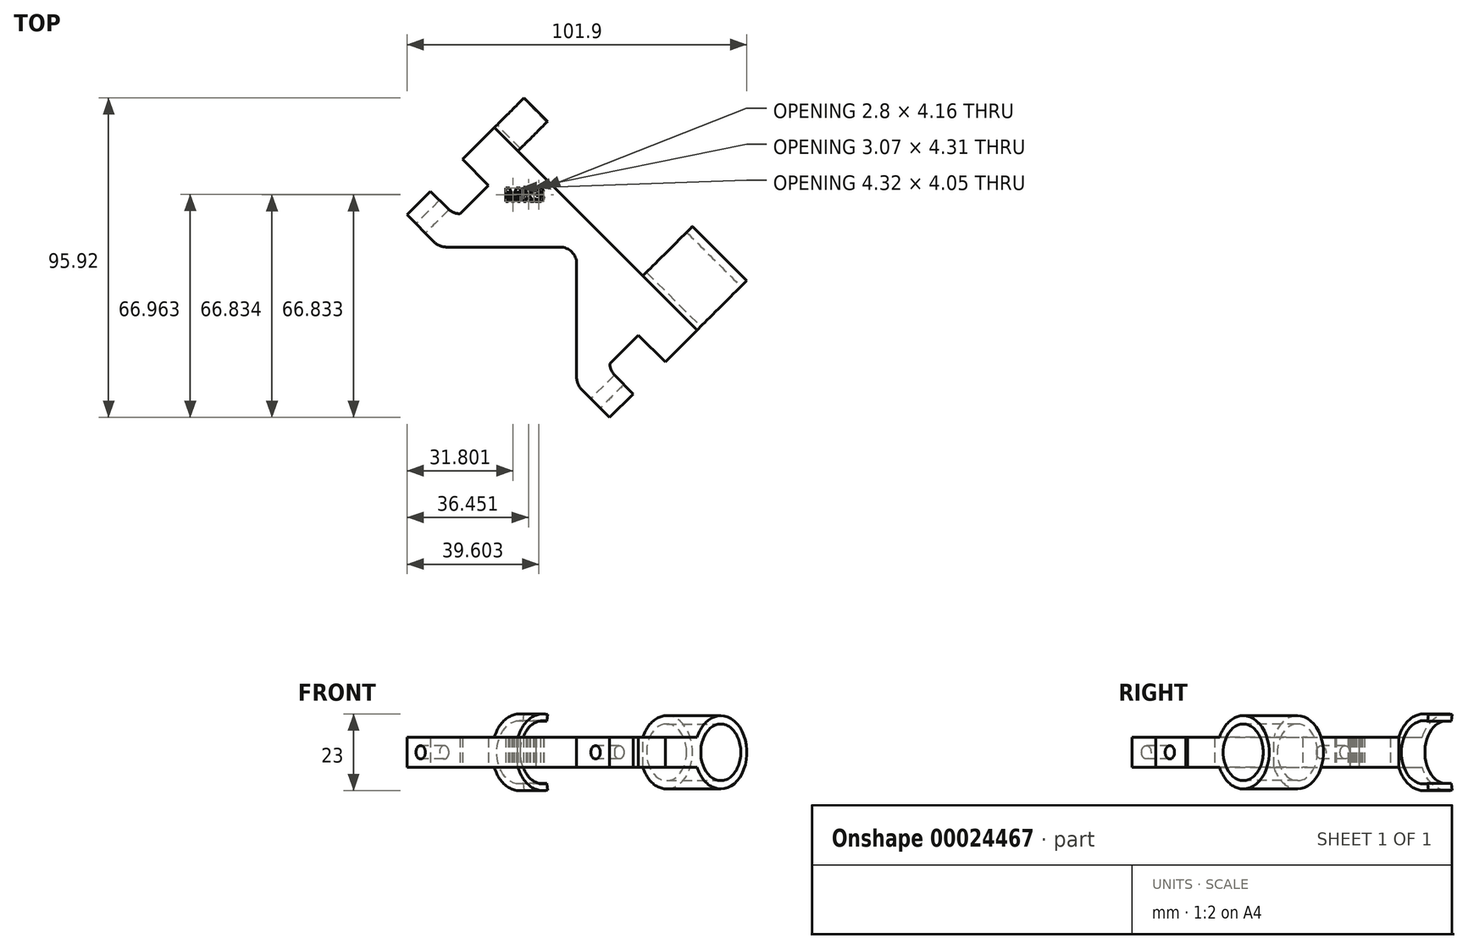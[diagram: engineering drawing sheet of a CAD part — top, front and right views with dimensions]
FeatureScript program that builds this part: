
annotation { "Feature Type Name" : "Feature", "Feature Type Description" : "" }
export const myFeature = defineFeature(function(context is Context, id is Id, definition is map)
    precondition{}
    {
        {
            var Q0;
            Q0=qCreatedBy(makeId("Top.planeOp"),FACE);
            var sketch = newSketch(context, id + "F0", { "sketchPlane" : qUnion([Q0])});
            skLineSegment(sketch, "E0.bottom", {"start": v(-27.06, 13.99) * mm, "end": v(8.94, 13.99) * mm});
            skLineSegment(sketch, "E0.right", {"start": v(13.94, 8.99) * mm, "end": v(13.94, -27.01) * mm});
            skPoint(sketch, "E1.visualSharp", {"position": v(13.94, 13.99) * mm});
            skArc(sketch, "E1.filletArc", {"start": v(13.94, 8.99) * mm, "mid": v(12.48, 12.52) * mm, "end": v(8.94, 13.99) * mm});
            skLineSegment(sketch, "E2.0", {"start": v(23.94, 8.99) * mm, "end": v(23.94, -21.01) * mm});
            skArc(sketch, "E2.1", {"start": v(23.94, 8.99) * mm, "mid": v(19.55, 19.6) * mm, "end": v(8.94, 23.99) * mm});
            skLineSegment(sketch, "E2.2", {"start": v(-21.06, 23.99) * mm, "end": v(8.94, 23.99) * mm});
            skLineSegment(sketch, "E3", {"start": v(-24.6, 25.45) * mm, "end": v(-29.87, 30.73) * mm});
            skLineSegment(sketch, "E4.0", {"start": v(-30.2, 16.92) * mm, "end": v(-36.94, 23.66) * mm});
            skLineSegment(sketch, "E5", {"start": v(-30.2, 16.92) * mm, "end": v(-28.73, 15.45) * mm});
            skLineSegment(sketch, "E6", {"start": v(-25.2, 13.99) * mm, "end": v(-27.06, 13.99) * mm});
            skLineSegment(sketch, "E7", {"start": v(-36.94, 23.66) * mm, "end": v(-29.87, 30.73) * mm});
            skPoint(sketch, "E8.visualSharp", {"position": v(-23.13, 23.99) * mm});
            skArc(sketch, "E8.filletArc", {"start": v(-24.6, 25.45) * mm, "mid": v(-22.97, 24.37) * mm, "end": v(-21.06, 23.99) * mm});
            skPoint(sketch, "E9.visualSharp", {"position": v(-27.27, 13.99) * mm});
            skArc(sketch, "E9.filletArc", {"start": v(-28.73, 15.45) * mm, "mid": v(-27.11, 14.37) * mm, "end": v(-25.2, 13.99) * mm});
            skLineSegment(sketch, "E10", {"start": v(25.4, -24.55) * mm, "end": v(30.94, -30.08) * mm});
            skLineSegment(sketch, "E11.0", {"start": v(16.87, -30.16) * mm, "end": v(23.87, -37.16) * mm});
            skLineSegment(sketch, "E12", {"start": v(13.94, -25.16) * mm, "end": v(13.94, -27.01) * mm});
            skLineSegment(sketch, "E13", {"start": v(16.87, -30.16) * mm, "end": v(15.4, -28.7) * mm});
            skPoint(sketch, "E14.visualSharp", {"position": v(13.94, -27.23) * mm});
            skArc(sketch, "E14.filletArc", {"start": v(13.94, -25.16) * mm, "mid": v(14.33, -27.07) * mm, "end": v(15.4, -28.7) * mm});
            skPoint(sketch, "E15.visualSharp", {"position": v(23.94, -23.08) * mm});
            skArc(sketch, "E15.filletArc", {"start": v(23.94, -21.01) * mm, "mid": v(24.33, -22.93) * mm, "end": v(25.4, -24.55) * mm});
            skLineSegment(sketch, "E16", {"start": v(30.94, -30.08) * mm, "end": v(23.87, -37.16) * mm});
            skLineSegment(sketch, "E17", {"start": v(19.55, 19.6) * mm, "end": v(50.09, -10.94) * mm});
            skLineSegment(sketch, "E18", {"start": v(40.52, -20.51) * mm, "end": v(50.09, -10.94) * mm});
            skLineSegment(sketch, "E19", {"start": v(-20.3, 40.3) * mm, "end": v(-10.72, 49.87) * mm});
            skLineSegment(sketch, "E20", {"start": v(19.55, 19.6) * mm, "end": v(-10.72, 49.87) * mm});
            skLineSegment(sketch, "E21", {"start": v(-20.3, 40.3) * mm, "end": v(-13.56, 33.56) * mm});
            skLineSegment(sketch, "E22", {"start": v(-23.13, 23.99) * mm, "end": v(-22.8, 24.3) * mm});
            skLineSegment(sketch, "E23", {"start": v(40.52, -20.51) * mm, "end": v(33.52, -13.51) * mm});
            skLineSegment(sketch, "E24", {"start": v(23.94, -23.08) * mm, "end": v(24.26, -22.77) * mm});
            skLineSegment(sketch, "E25", {"start": v(23.94, -21.01) * mm, "end": v(32.48, -12.48) * mm});
            skLineSegment(sketch, "E26", {"start": v(33.52, -13.51) * mm, "end": v(32.48, -12.48) * mm});
            skLineSegment(sketch, "E27", {"start": v(-21.06, 23.99) * mm, "end": v(-12.52, 32.52) * mm});
            skLineSegment(sketch, "E28", {"start": v(-13.56, 33.56) * mm, "end": v(-12.52, 32.52) * mm});
            skText(sketch, "E29", { "text": "Mk3", "fontName": "OpenSans-Bold.ttf"});
            skPoint(sketch, "E29.secondSnap0", {"position": v(4.41, 34.73) * mm});
            const initialGuessF0  = {"E29": [-0.00781, 0.02765, 1, 0, 0.00408]};
            skSetInitialGuess(sketch, initialGuessF0);
            skSolve(sketch);
        }
        {
            var Q0;
            Q0=makeQuery(id+"F0.imprint","IMPRINT",FACE,{"disambiguationData":[TD([[makeQuery(id+"F0.imprint","IMPRINT",EDGE,{"derivedFrom":sQuery(id+"F0.wireOp",EDGE,"E0.bottom")}),1.0]])]});
            var Q1;
            {var subQ0=sQuery(id+"F0.wireOp",EDGE,"E2.2");Q1=makeQuery(id+"F0.imprint","IMPRINT",FACE,{"disambiguationData":[TD([[makeQuery(id+"F0.imprint","IMPRINT",EDGE,{"derivedFrom":subQ0}),1.0]])]});}
            var Q2;
            {var subQ1=sQuery(id+"F0.wireOp",EDGE,"E2.0");Q2=makeQuery(id+"F0.imprint","IMPRINT",FACE,{"disambiguationData":[TD([[makeQuery(id+"F0.imprint","IMPRINT",EDGE,{"derivedFrom":subQ1}),1.0]])]});}
            extrude(context, id + "F1", {"entities" : qUnion([Q0, Q1, Q2]), "depth" : 9 * mm});
        }
        {
            var Q0;
            Q0=makeQuery(id+"F1.opExtrude","SWEPT_FACE",FACE,{"disambiguationData":[OSD([sQuery(id+"F0.wireOp",EDGE,"E16"),sQuery(id+"F0.wireOp",EDGE,"E18")])]});
            var sketch = newSketch(context, id + "F2", { "sketchPlane" : qUnion([Q0])});
            skCircle(sketch, "E30", {"center": v(37.72, 4.5) * mm, "radius": 11 * mm});
            skPoint(sketch, "E30.first.point", {"position": v(27.68, 9) * mm});
            skPoint(sketch, "E30.second.point", {"position": v(27.68, 0) * mm});
            skPoint(sketch, "E30.third.point", {"position": v(47.75, 9) * mm});
            skCircle(sketch, "E31", {"center": v(37.72, 4.5) * mm, "radius": 8.5 * mm});
            skSolve(sketch);
        }
        {
            var Q0;
            Q0 = qSketchRegion(id + "F2", true);
            var Q1;
            Q1=makeQuery(id+"F1.opExtrude","SWEPT_FACE",FACE,{"disambiguationData":[OSD([sQuery(id+"F0.wireOp",EDGE,"E7"),sQuery(id+"F0.wireOp",EDGE,"E19")])]});
            extrude(context, id + "F3", {"entities" : qUnion([Q0]), "operationType" : NewBodyOperationType.ADD, "oppositeDirection" : true, "endBoundEntityFace" : qUnion([Q1]), "depth" : 23 * mm});
        }
        {
            var Q0;
            Q0=makeQuery(id+"F1.opExtrude","SWEPT_FACE",FACE,{"disambiguationData":[OSD([sQuery(id+"F0.wireOp",EDGE,"E4.0"),sQuery(id+"F0.wireOp",EDGE,"E5")])]});
            var sketch = newSketch(context, id + "F4", { "sketchPlane" : qUnion([Q0])});
            skPoint(sketch, "E32", {"position": v(-37.04, 4.5) * mm});
            skPoint(sketch, "E32.positionSnap0", {"position": v(-37.04, 9) * mm});
            skPoint(sketch, "E32.positionSnap1", {"position": v(-42.85, 4.5) * mm});
            skSolve(sketch);
        }
        {
            var Q0;
            Q0=sQuery(id+"F4.wireOp",VERTEX,"E32");
            var Q1;
            Q1=makeQuery(id+"F1.opExtrude","SWEPT_BODY",BODY,{"disambiguationData":[OSD([sQuery(id+"F0.wireOp",EDGE,"E0.bottom"),sQuery(id+"F0.wireOp",EDGE,"E0.right"),sQuery(id+"F0.wireOp",EDGE,"E1.filletArc"),sQuery(id+"F0.wireOp",EDGE,"E3"),sQuery(id+"F0.wireOp",EDGE,"E4.0"),sQuery(id+"F0.wireOp",EDGE,"E5"),sQuery(id+"F0.wireOp",EDGE,"E7"),sQuery(id+"F0.wireOp",EDGE,"E8.filletArc"),sQuery(id+"F0.wireOp",EDGE,"E9.filletArc"),sQuery(id+"F0.wireOp",EDGE,"E10"),sQuery(id+"F0.wireOp",EDGE,"E11.0"),sQuery(id+"F0.wireOp",EDGE,"E13"),sQuery(id+"F0.wireOp",EDGE,"E14.filletArc"),sQuery(id+"F0.wireOp",EDGE,"E15.filletArc"),sQuery(id+"F0.wireOp",EDGE,"E16"),sQuery(id+"F0.wireOp",EDGE,"E17"),sQuery(id+"F0.wireOp",EDGE,"E18"),sQuery(id+"F0.wireOp",EDGE,"E19"),sQuery(id+"F0.wireOp",EDGE,"E20"),sQuery(id+"F0.wireOp",EDGE,"E21"),sQuery(id+"F0.wireOp",EDGE,"E22"),sQuery(id+"F0.wireOp",EDGE,"E23"),sQuery(id+"F0.wireOp",EDGE,"E24")])]});
            hole(context, id + "F5", {"style" : HoleStyle.SIMPLE, "endStyle" : HoleEndStyle.BLIND, "holeDiameter" : 4 * mm, "holeDepth" : 20 * mm, "locations" : qUnion([Q0]), "scope" : qUnion([Q1])});
        }
        {
            var Q0;
            Q0=makeQuery(id+"F1.opExtrude","SWEPT_FACE",FACE,{"disambiguationData":[OSD([sQuery(id+"F0.wireOp",EDGE,"E11.0"),sQuery(id+"F0.wireOp",EDGE,"E13")])]});
            var sketch = newSketch(context, id + "F6", { "sketchPlane" : qUnion([Q0])});
            skPoint(sketch, "E33", {"position": v(37.17, 4.5) * mm});
            skPoint(sketch, "E33.positionSnap0", {"position": v(43.15, 4.5) * mm});
            skPoint(sketch, "E33.positionSnap1", {"position": v(37.17, 0) * mm});
            skSolve(sketch);
        }
        {
            var Q0;
            Q0=sQuery(id+"F6.wireOp",VERTEX,"E33");
            var Q1;
            Q1=makeQuery(id+"F1.opExtrude","SWEPT_BODY",BODY,{"disambiguationData":[OSD([sQuery(id+"F0.wireOp",EDGE,"E0.bottom"),sQuery(id+"F0.wireOp",EDGE,"E0.right"),sQuery(id+"F0.wireOp",EDGE,"E1.filletArc"),sQuery(id+"F0.wireOp",EDGE,"E3"),sQuery(id+"F0.wireOp",EDGE,"E4.0"),sQuery(id+"F0.wireOp",EDGE,"E5"),sQuery(id+"F0.wireOp",EDGE,"E7"),sQuery(id+"F0.wireOp",EDGE,"E8.filletArc"),sQuery(id+"F0.wireOp",EDGE,"E9.filletArc"),sQuery(id+"F0.wireOp",EDGE,"E10"),sQuery(id+"F0.wireOp",EDGE,"E11.0"),sQuery(id+"F0.wireOp",EDGE,"E13"),sQuery(id+"F0.wireOp",EDGE,"E14.filletArc"),sQuery(id+"F0.wireOp",EDGE,"E15.filletArc"),sQuery(id+"F0.wireOp",EDGE,"E16"),sQuery(id+"F0.wireOp",EDGE,"E17"),sQuery(id+"F0.wireOp",EDGE,"E18"),sQuery(id+"F0.wireOp",EDGE,"E19"),sQuery(id+"F0.wireOp",EDGE,"E20"),sQuery(id+"F0.wireOp",EDGE,"E21"),sQuery(id+"F0.wireOp",EDGE,"E22"),sQuery(id+"F0.wireOp",EDGE,"E23"),sQuery(id+"F0.wireOp",EDGE,"E24")])]});
            hole(context, id + "F7", {"style" : HoleStyle.SIMPLE, "endStyle" : HoleEndStyle.BLIND, "holeDiameter" : 4 * mm, "holeDepth" : 20 * mm, "locations" : qUnion([Q0]), "scope" : qUnion([Q1])});
        }
        {
            var Q0;
            Q0=makeQuery(id+"F1.opExtrude","SWEPT_FACE",FACE,{"disambiguationData":[OSD([sQuery(id+"F0.wireOp",EDGE,"E19")])]});
            var sketch = newSketch(context, id + "F8", { "sketchPlane" : qUnion([Q0])});
            skArc(sketch, "E34", {"start": v(-40.26, -6.83) * mm, "mid": v(-26.76, 4.5) * mm, "end": v(-40.26, 15.83) * mm});
            skPoint(sketch, "E34.first.point", {"position": v(-27.68, 9) * mm});
            skPoint(sketch, "E34.second.point", {"position": v(-27.68, 0) * mm});
            skPoint(sketch, "E34.third.point", {"position": v(-49.63, 6.25) * mm});
            skArc(sketch, "E35.0", {"start": v(-39.91, -4.86) * mm, "mid": v(-28.76, 4.5) * mm, "end": v(-39.91, 13.86) * mm});
            skLineSegment(sketch, "E36", {"start": v(-39.91, -4.86) * mm, "end": v(-40.26, -6.83) * mm});
            skLineSegment(sketch, "E37", {"start": v(-39.91, 13.86) * mm, "end": v(-40.26, 15.83) * mm});
            skSolve(sketch);
        }
        {
            var Q0;
            Q0=makeQuery(id+"F8.imprint","IMPRINT",FACE,{"disambiguationData":[TD([[makeQuery(id+"F8.imprint","IMPRINT",EDGE,{"derivedFrom":sQuery(id+"F8.wireOp",EDGE,"E35.0")}),-1.0]])]});
            extrude(context, id + "F9", {"entities" : qUnion([Q0]), "operationType" : NewBodyOperationType.ADD, "oppositeDirection" : true, "depth" : 10 * mm});
        }
    });
